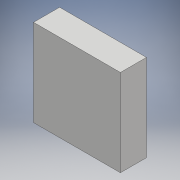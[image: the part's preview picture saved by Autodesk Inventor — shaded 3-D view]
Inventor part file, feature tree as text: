
AUTODESK INVENTOR PART (.ipt)
format: ipt  version: 2017 (Build 210142000, 142)  size: 96,256 bytes
history: native  units: mm
features: extrude x1, sketch x1
ambient origin geometry x8: Origin, YZ Plane, XZ Plane, XY Plane, X Axis, Y Axis, Z Axis, Center Point
bodies: Solid1 (feature_tree)
feature tree (2):
  extrude  "Extrusion1"  Depth=50.0mm
  sketch  "Sketch1"  dims[d0=50.0mm d1=50.0mm d2=15.0mm d3=0.0mm]
